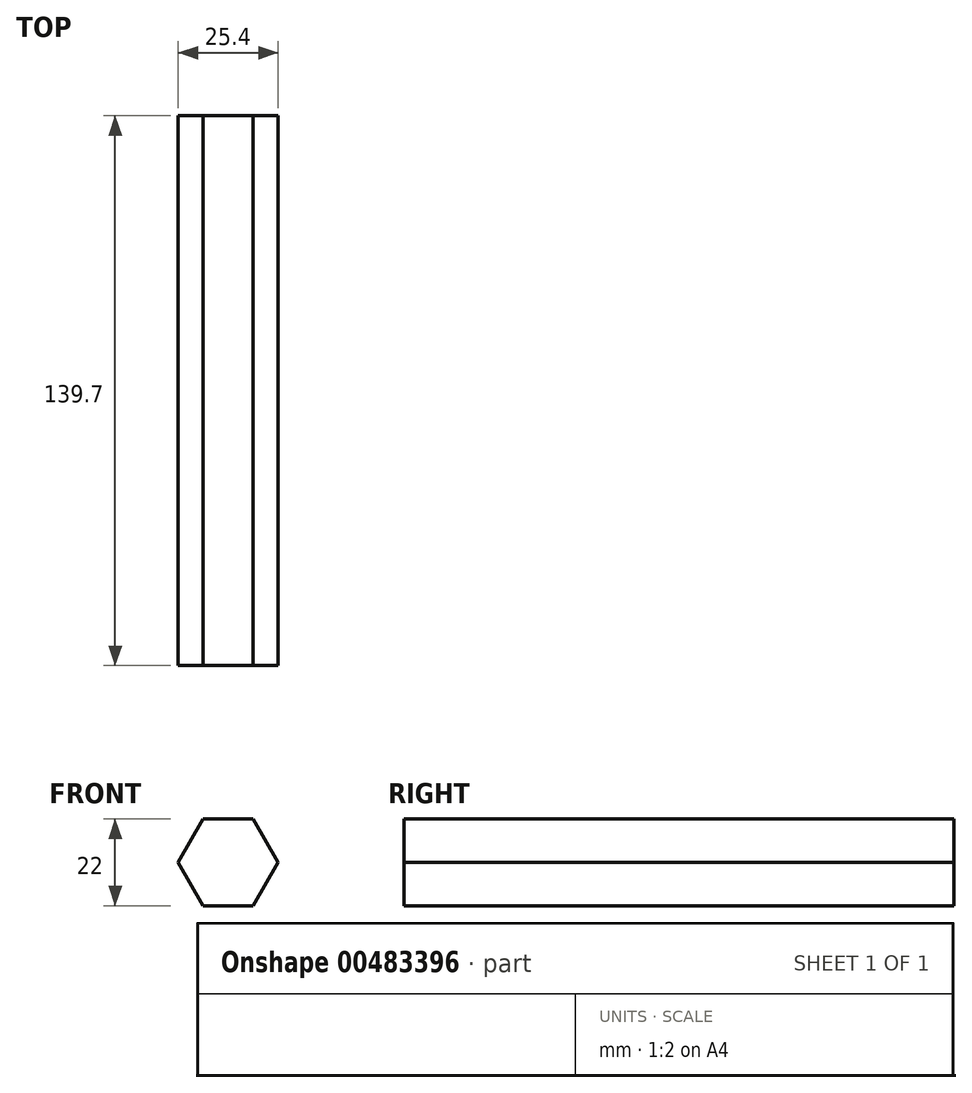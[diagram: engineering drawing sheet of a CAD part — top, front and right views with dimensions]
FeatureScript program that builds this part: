
annotation { "Feature Type Name" : "Feature", "Feature Type Description" : "" }
export const myFeature = defineFeature(function(context is Context, id is Id, definition is map)
    precondition{}
    {
        {
            var Q0;
            Q0=qCreatedBy(makeId("Front.planeOp"),FACE);
            var sketch = newSketch(context, id + "F0", { "sketchPlane" : qUnion([Q0])});
            skCircle(sketch, "E0.cCircle", {"center": v(0, 0) * mm, "radius": 12.7 * mm, "construction": true});
            skLineSegment(sketch, "E0.0", {"start": v(6.35, -11) * mm, "end": v(-6.35, -11) * mm});
            skLineSegment(sketch, "E0.1", {"start": v(-6.35, -11) * mm, "end": v(-12.7, 0) * mm});
            skLineSegment(sketch, "E0.2", {"start": v(-12.7, 0) * mm, "end": v(-6.35, 11) * mm});
            skLineSegment(sketch, "E0.3", {"start": v(-6.35, 11) * mm, "end": v(6.35, 11) * mm});
            skLineSegment(sketch, "E0.4", {"start": v(6.35, 11) * mm, "end": v(12.7, 0) * mm});
            skLineSegment(sketch, "E0.5", {"start": v(12.7, 0) * mm, "end": v(6.35, -11) * mm});
            skSolve(sketch);
        }
        {
            var Q0;
            Q0 = qSketchRegion(id + "F0", true);
            extrude(context, id + "F1", {"entities" : qUnion([Q0]), "depth" : 139.7 * mm});
        }
    });
